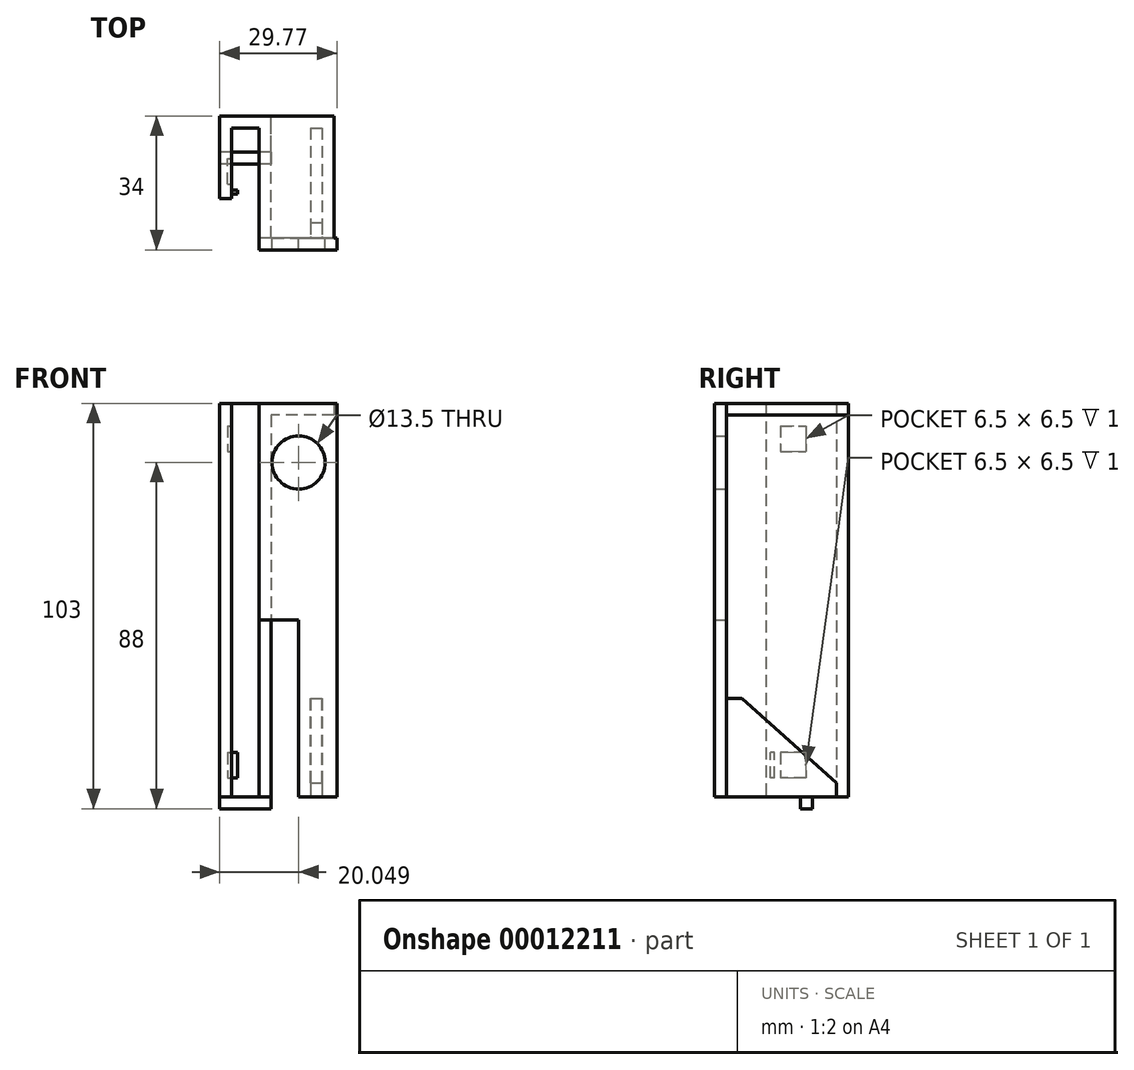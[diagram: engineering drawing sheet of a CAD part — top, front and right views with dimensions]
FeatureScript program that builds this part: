
annotation { "Feature Type Name" : "Feature", "Feature Type Description" : "" }
export const myFeature = defineFeature(function(context is Context, id is Id, definition is map)
    precondition{}
    {
        {
            var Q0;
            Q0=qCreatedBy(makeId("Top.planeOp"),FACE);
            var sketch = newSketch(context, id + "F0", { "sketchPlane" : qUnion([Q0])});
            skLineSegment(sketch, "E0", {"start": v(-54.2, 35.8) * mm, "end": v(-54.2, 56.8) * mm});
            skLineSegment(sketch, "E1", {"start": v(-54.2, 56.8) * mm, "end": v(-41.2, 56.8) * mm});
            skLineSegment(sketch, "E2", {"start": v(-41.2, 56.8) * mm, "end": v(-41.2, 25.8) * mm});
            skLineSegment(sketch, "E3", {"start": v(-41.2, 25.8) * mm, "end": v(-24.44, 25.8) * mm});
            skLineSegment(sketch, "E4", {"start": v(-54.2, 35.8) * mm, "end": v(-51.2, 35.8) * mm});
            skLineSegment(sketch, "E5", {"start": v(-51.2, 35.8) * mm, "end": v(-51.2, 53.8) * mm});
            skLineSegment(sketch, "E6", {"start": v(-51.2, 53.8) * mm, "end": v(-44.2, 53.8) * mm});
            skLineSegment(sketch, "E7", {"start": v(-44.2, 53.8) * mm, "end": v(-44.2, 22.8) * mm});
            skLineSegment(sketch, "E8", {"start": v(-44.2, 22.8) * mm, "end": v(-24.44, 22.8) * mm});
            skLineSegment(sketch, "E9", {"start": v(-24.44, 22.8) * mm, "end": v(-24.44, 25.8) * mm});
            skSolve(sketch);
        }
        {
            var Q0;
            Q0=makeQuery(id+"F0.imprint","IMPRINT",FACE,{"disambiguationData":[TD([[makeQuery(id+"F0.imprint","IMPRINT",EDGE,{"derivedFrom":sQuery(id+"F0.wireOp",EDGE,"E0")}),-1.0]])]});
            var Q1;
            Q1 = qSketchRegion(id + "F2", true);
            extrude(context, id + "F1", {"entities" : qUnion([Q0, Q1]), "depth" : 100 * mm});
        }
        {
            var Q0;
            Q0=makeQuery(id+"F1.opExtrude","SWEPT_FACE",FACE,{"disambiguationData":[OSD([sQuery(id+"F0.wireOp",EDGE,"E3")])]});
            var sketch = newSketch(context, id + "F2", { "sketchPlane" : qUnion([Q0])});
            skLineSegment(sketch, "E10.bottom", {"start": v(34.2, 45) * mm, "end": v(54.66, 45) * mm});
            skLineSegment(sketch, "E10.top", {"start": v(34.2, -6.64) * mm, "end": v(54.66, -6.64) * mm});
            skLineSegment(sketch, "E10.left", {"start": v(34.2, 45) * mm, "end": v(34.2, -6.64) * mm});
            skLineSegment(sketch, "E10.right", {"start": v(54.66, 45) * mm, "end": v(54.66, -6.64) * mm});
            skCircle(sketch, "E11", {"center": v(34.16, 85) * mm, "radius": 6.75 * mm});
            skSolve(sketch);
        }
        {
            var Q0;
            Q0 = qSketchRegion(id + "F2", true);
            extrude(context, id + "F3", {"entities" : qUnion([Q0]), "operationType" : NewBodyOperationType.REMOVE, "oppositeDirection" : true, "depth" : 25 * mm});
        }
        {
            var Q0;
            Q0=makeQuery(id+"F1.opExtrude","SWEPT_FACE",FACE,{"disambiguationData":[OSD([sQuery(id+"F0.wireOp",EDGE,"E5")])]});
            var sketch = newSketch(context, id + "F4", { "sketchPlane" : qUnion([Q0])});
            skLineSegment(sketch, "E12.bottom", {"start": v(46, 11.3) * mm, "end": v(39.5, 11.3) * mm});
            skLineSegment(sketch, "E12.top", {"start": v(46, 4.8) * mm, "end": v(39.5, 4.8) * mm});
            skLineSegment(sketch, "E12.left", {"start": v(46, 11.3) * mm, "end": v(46, 4.8) * mm});
            skLineSegment(sketch, "E12.right", {"start": v(39.5, 11.3) * mm, "end": v(39.5, 4.8) * mm});
            skLineSegment(sketch, "E13.bottom", {"start": v(39.5, 94.3) * mm, "end": v(46, 94.3) * mm});
            skLineSegment(sketch, "E13.top", {"start": v(39.5, 87.8) * mm, "end": v(46, 87.8) * mm});
            skLineSegment(sketch, "E13.left", {"start": v(39.5, 94.3) * mm, "end": v(39.5, 87.8) * mm});
            skLineSegment(sketch, "E13.right", {"start": v(46, 94.3) * mm, "end": v(46, 87.8) * mm});
            skSolve(sketch);
        }
        {
            var Q0;
            Q0 = qSketchRegion(id + "F4", true);
            extrude(context, id + "F5", {"entities" : qUnion([Q0]), "operationType" : NewBodyOperationType.REMOVE, "oppositeDirection" : true, "depth" : 1 * mm});
        }
        {
            var Q0;
            Q0=makeQuery(id+"F1.opExtrude","SWEPT_FACE",FACE,{"disambiguationData":[OSD([sQuery(id+"F0.wireOp",EDGE,"E2")])]});
            var sketch = newSketch(context, id + "F6", { "sketchPlane" : qUnion([Q0])});
            skLineSegment(sketch, "E14.bottom", {"start": v(25.8, 97) * mm, "end": v(56.8, 97) * mm});
            skLineSegment(sketch, "E14.top", {"start": v(25.8, 100) * mm, "end": v(56.8, 100) * mm});
            skLineSegment(sketch, "E14.left", {"start": v(25.8, 97) * mm, "end": v(25.8, 100) * mm});
            skLineSegment(sketch, "E14.right", {"start": v(56.8, 97) * mm, "end": v(56.8, 100) * mm});
            skSolve(sketch);
        }
        {
            var Q0;
            Q0=makeQuery(id+"F6.imprint","IMPRINT",FACE,{"disambiguationData":[TD([[makeQuery(id+"F6.imprint","IMPRINT",EDGE,{"derivedFrom":sQuery(id+"F6.wireOp",EDGE,"E14.bottom")}),1.0]])]});
            extrude(context, id + "F7", {"entities" : qUnion([Q0]), "operationType" : NewBodyOperationType.ADD, "depth" : 16 * mm});
        }
        {
            var Q0;
            Q0=makeQuery(id+"F1.opExtrude","SWEPT_FACE",FACE,{"disambiguationData":[OSD([sQuery(id+"F0.wireOp",EDGE,"E3")])]});
            var sketch = newSketch(context, id + "F8", { "sketchPlane" : qUnion([Q0])});
            skLineSegment(sketch, "E15.bottom", {"start": v(31.2, 25) * mm, "end": v(28.2, 25) * mm});
            skLineSegment(sketch, "E15.top", {"start": v(31.2, 0) * mm, "end": v(28.2, 0) * mm});
            skLineSegment(sketch, "E15.left", {"start": v(31.2, 25) * mm, "end": v(31.2, 0) * mm});
            skLineSegment(sketch, "E15.right", {"start": v(28.2, 25) * mm, "end": v(28.2, 0) * mm});
            skSolve(sketch);
        }
        {
            var Q0;
            Q0 = qSketchRegion(id + "F8", true);
            extrude(context, id + "F9", {"entities" : qUnion([Q0]), "operationType" : NewBodyOperationType.ADD, "depth" : 28 * mm});
        }
        {
            var Q0;
            Q0=makeQuery(id+"F9.opExtrude","SWEPT_FACE",FACE,{"disambiguationData":[OSD([sQuery(id+"F8.wireOp",EDGE,"E15.right")])]});
            var sketch = newSketch(context, id + "F10", { "sketchPlane" : qUnion([Q0])});
            skLineSegment(sketch, "E16", {"start": v(53.8, 25) * mm, "end": v(53.8, 3.61) * mm});
            skLineSegment(sketch, "E17", {"start": v(53.8, 3.61) * mm, "end": v(29.73, 25) * mm});
            skLineSegment(sketch, "E18", {"start": v(29.73, 25) * mm, "end": v(53.8, 25) * mm});
            skSolve(sketch);
        }
        {
            var Q0;
            Q0 = qSketchRegion(id + "F10", true);
            extrude(context, id + "F11", {"entities" : qUnion([Q0]), "operationType" : NewBodyOperationType.REMOVE, "oppositeDirection" : true, "depth" : 3 * mm});
        }
        {
            var Q0;
            Q0=makeQuery(id+"F0.imprint","IMPRINT",FACE,{"disambiguationData":[TD([[makeQuery(id+"F0.imprint","IMPRINT",EDGE,{"derivedFrom":sQuery(id+"F0.wireOp",EDGE,"E0")}),-1.0]])]});
            var sketch = newSketch(context, id + "F12", { "sketchPlane" : qUnion([Q0])});
            skLineSegment(sketch, "E19.bottom", {"start": v(-41.21, 47.62) * mm, "end": v(-54.21, 47.62) * mm});
            skLineSegment(sketch, "E19.top", {"start": v(-41.21, 44.62) * mm, "end": v(-54.21, 44.62) * mm});
            skLineSegment(sketch, "E19.left", {"start": v(-41.21, 47.62) * mm, "end": v(-41.21, 44.62) * mm});
            skLineSegment(sketch, "E19.right", {"start": v(-54.21, 47.62) * mm, "end": v(-54.21, 44.62) * mm});
            skSolve(sketch);
        }
        {
            var Q0;
            Q0 = qSketchRegion(id + "F12", true);
            var Q1;
            Q1 = qSketchRegion(id + "F14", true);
            extrude(context, id + "F13", {"entities" : qUnion([Q0, Q1]), "operationType" : NewBodyOperationType.ADD, "oppositeDirection" : true, "depth" : 3 * mm});
        }
        {
            var Q0;
            Q0=makeQuery(id+"F1.opExtrude","SWEPT_FACE",FACE,{"disambiguationData":[OSD([sQuery(id+"F0.wireOp",EDGE,"E5")])]});
            var sketch = newSketch(context, id + "F14", { "sketchPlane" : qUnion([Q0])});
            skLineSegment(sketch, "E20.bottom", {"start": v(38.04, 4.8) * mm, "end": v(37.04, 4.8) * mm});
            skLineSegment(sketch, "E20.top", {"start": v(38.04, 11.3) * mm, "end": v(37.04, 11.3) * mm});
            skLineSegment(sketch, "E20.left", {"start": v(38.04, 4.8) * mm, "end": v(38.04, 11.3) * mm});
            skLineSegment(sketch, "E20.right", {"start": v(37.04, 4.8) * mm, "end": v(37.04, 11.3) * mm});
            skSolve(sketch);
        }
        {
            var Q0;
            Q0 = qSketchRegion(id + "F14", true);
            extrude(context, id + "F15", {"entities" : qUnion([Q0]), "operationType" : NewBodyOperationType.ADD, "depth" : 1.5 * mm});
        }
    });
